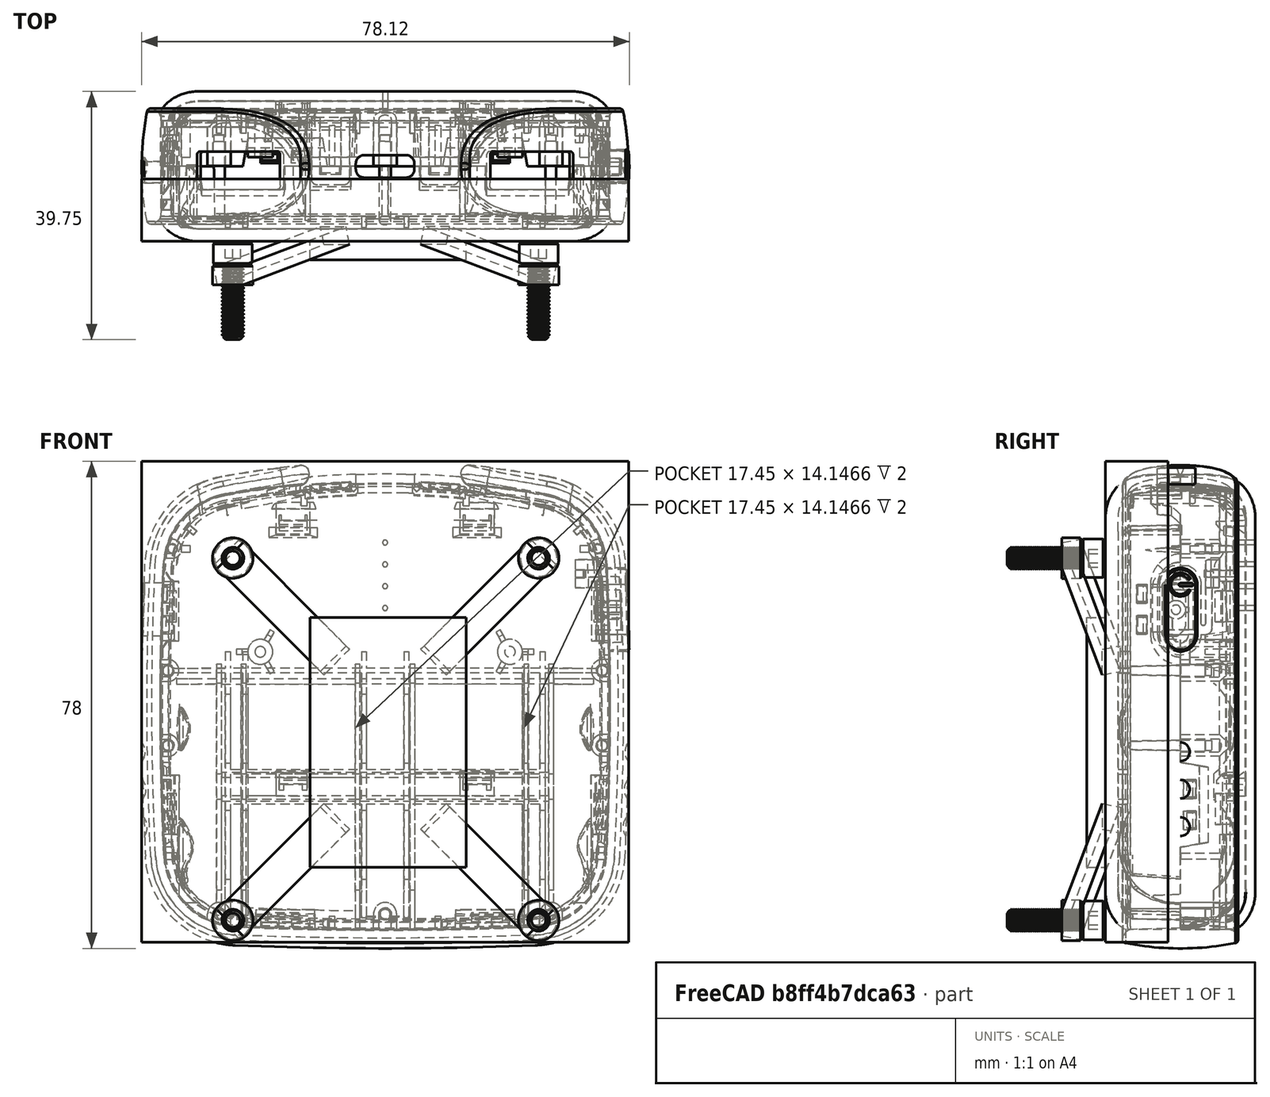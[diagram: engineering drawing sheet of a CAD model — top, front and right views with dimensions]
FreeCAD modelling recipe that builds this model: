
FCSTD DOCUMENT  (FreeCAD 0.20R29410 (Git))
Label: wearableV2_01_09_2023
License: All rights reserved
LicenseURL: http://en.wikipedia.org/wiki/All_rights_reserved
objects: Part::Feature×14, Part::MultiFuse×11, Part::Cylinder×4, Part::Box×3, App::Part×2, Part::Mirroring×2
note: 34 computed .brp shape members not serialized (recipe doc carries the construction recipe); baked Part::Feature solids carry a one-line shape summary decoded from their .brp

FEATURE [Part::Feature] Part__Feature  label="2_BAT_1_1"
  shape: bbox 14.52 x 64.97 x 15.41 mm, 79 faces (baked)
FEATURE [Part::Feature] Part__Feature001  label="2_C_1_1"
  shape: bbox 73.62 x 34.12 x 73.84 mm, 562 faces (baked)
FEATURE [Part::Feature] Part__Feature002  label="2_A_1_1"
  shape: bbox 73.61 x 58.23 x 73.83 mm, 215 faces (baked)
FEATURE [Part::Feature] Part__Feature003  label="2_B_2_1"
  shape: bbox 78.1 x 64.8 x 77.53 mm, 719 faces (baked)
FEATURE [Part::MultiFuse] Fusion
  Shapes = -> [Part__Feature003,Part__Feature002]
FEATURE [Part::MultiFuse] Fusion001
  Shapes = -> [Part__Feature001,Part__Feature]
FEATURE [Part::MultiFuse] Fusion002  label="V25"
  Placement = pos=(39,12,38) rot=(0,0,-1;3.14159rad)
  Shapes = -> [Fusion001,Fusion]
FEATURE [Part::Feature] Part__Feature004  label="Open CASCADE STEP translator 7.4 2.1.1"
  shape: bbox 8.3 x 1.9 x 1 mm, 10 faces, 0 solids (baked)
FEATURE [Part::Feature] Part__Feature005  label="Open CASCADE STEP translator 7.4 2.1.2"
  shape: bbox 12.5 x 10 x 1.5 mm, 6 faces, 0 solids (baked)
FEATURE [Part::Feature] Part__Feature006  label="Open CASCADE STEP translator 7.4 2.1.3"
  shape: bbox 12.5 x 10 x 1.5 mm, 6 faces, 0 solids (baked)
FEATURE [Part::Feature] Part__Feature007  label="Open CASCADE STEP translator 7.4 2.1.4"
  shape: bbox 12.5 x 10 x 1.5 mm, 6 faces, 0 solids (baked)
FEATURE [Part::Feature] Part__Feature008  label="Open CASCADE STEP translator 7.4 2.1.5"
  shape: bbox 12.5 x 10 x 1.5 mm, 6 faces, 0 solids (baked)
FEATURE [Part::Feature] Part__Feature009  label="Open CASCADE STEP translator 7.4 2.1.6"
  shape: bbox 89.5 x 57.1 x 20.65 mm, 2741 faces, 0 solids (baked)
FEATURE [App::Part] Open_CASCADE_STEP_translator_7_4_2_1  label="Open CASCADE STEP translator 7.4 2.1"
  Group = -> [Part__Feature004,Part__Feature005,Part__Feature006,Part__Feature007,Part__Feature008,Part__Feature009]
  Origin = -> Origin
FEATURE [App::Part] Open_CASCADE_STEP_translator_7_4_2  label="C4"
  Group = -> [Open_CASCADE_STEP_translator_7_4_2_1]
  Origin = -> Origin001
  Placement = pos=(67,-7,0) rot=(0.57735,-0.57735,0.57735;2.0944rad)
FEATURE [Part::Box] Box  label="Cube"
  AttacherType = Attacher::AttachEngine3D
  Height = 77
  Length = 78
  Width = 10
FEATURE [Part::Feature] Part__Feature010  label="m312mm"
  Placement = pos=(63.5,-7,61.5) rot=(0,-0.707107,-0.707107;3.14159rad)
  shape: bbox 6.201 x 15.54 x 6.201 mm, 70 faces (baked)
FEATURE [Part::Feature] Part__Feature011  label="m312mm001"
  Placement = pos=(14.5,-7,61.5) rot=(-1,0,0;1.5708rad)
  shape: bbox 6.201 x 15.54 x 6.201 mm, 70 faces (baked)
FEATURE [Part::MultiFuse] Fusion003
  Shapes = -> [Part__Feature011,Part__Feature010]
FEATURE [Part::Feature] Part__Feature012  label="m312mm002"
  Placement = pos=(14.5,-7,61.5) rot=(-1,0,0;1.5708rad)
  shape: bbox 6.201 x 15.54 x 6.201 mm, 70 faces (baked)
FEATURE [Part::Feature] Part__Feature013  label="m312mm003"
  Placement = pos=(63.5,-7,61.5) rot=(0,0.707107,0.707107;3.14159rad)
  shape: bbox 6.201 x 15.54 x 6.201 mm, 70 faces (baked)
FEATURE [Part::MultiFuse] Fusion004
  Placement = pos=(0,0,-58) rot=(0,0,1;0rad)
  Shapes = -> [Part__Feature012,Part__Feature013]
FEATURE [Part::MultiFuse] Fusion005
  Placement = pos=(0.1,-1,0) rot=(0,0,1;0rad)
  Shapes = -> [Fusion004,Fusion003]
FEATURE [Part::Box] Box001  label="Cube001"
  AttacherType = Attacher::AttachEngine3D
  Height = 40
  Length = 25
  Placement = pos=(27,-3,12) rot=(0,0,1;0rad)
  Width = 3
FEATURE [Part::Cylinder] Cylinder
  Angle = 360
  AttacherType = Attacher::AttachEngine3D
  FirstAngle = 0
  Height = 3
  Placement = pos=(14.5,-7,3.5) rot=(1,0,0;4.71239rad)
  Radius = 3.25
  SecondAngle = 0
FEATURE [Part::Cylinder] Cylinder001
  Angle = 360
  AttacherType = Attacher::AttachEngine3D
  FirstAngle = 0
  Height = 3
  Placement = pos=(63.5,-7,3.5) rot=(-1,0,0;1.5708rad)
  Radius = 3.25
  SecondAngle = 0
FEATURE [Part::MultiFuse] Fusion006
  Shapes = -> [Cylinder,Cylinder001]
FEATURE [Part::Cylinder] Cylinder002
  Angle = 360
  AttacherType = Attacher::AttachEngine3D
  FirstAngle = 0
  Height = 3
  Placement = pos=(14.5,-7,3.5) rot=(-1,0,0;1.5708rad)
  Radius = 3.25
  SecondAngle = 0
FEATURE [Part::Cylinder] Cylinder003
  Angle = 360
  AttacherType = Attacher::AttachEngine3D
  FirstAngle = 0
  Height = 3
  Placement = pos=(63.5,-7,3.5) rot=(-1,0,0;1.5708rad)
  Radius = 3.25
  SecondAngle = 0
FEATURE [Part::MultiFuse] Fusion007
  Placement = pos=(0,0,58) rot=(0,0,1;0rad)
  Shapes = -> [Cylinder002,Cylinder003]
FEATURE [Part::MultiFuse] Fusion008
  Placement = pos=(0.1,0,0) rot=(0,0,1;0rad)
  Shapes = -> [Fusion006,Fusion007]
FEATURE [Part::Box] Box002  label="Cube002"
  AttacherType = Attacher::AttachEngine3D
  Height = 25
  Length = 5.8
  Placement = pos=(12.12,-7,5.12) rot=(0.300549,-0.945607,-0.124491;5.45746rad)
  Width = 3
FEATURE [Part::Mirroring] Part__Mirroring  label="Cube002 (Mirror #1)"
  Base = (0,0,0)
  Normal = (0,0,1)
  Placement = pos=(0,0,65) rot=(0,0,1;0rad)
  Source = -> Box002
FEATURE [Part::MultiFuse] Fusion009
  Shapes = -> [Part__Mirroring,Box002]
FEATURE [Part::Mirroring] Part__Mirroring001  label="Fusion009 (Mirror #2)"
  Base = (0,0,0)
  Normal = (1,0,0)
  Placement = pos=(78,0,0) rot=(0,0,1;0rad)
  Source = -> Fusion009
FEATURE [Part::MultiFuse] Fusion010
  Shapes = -> [Fusion009,Part__Mirroring001]
